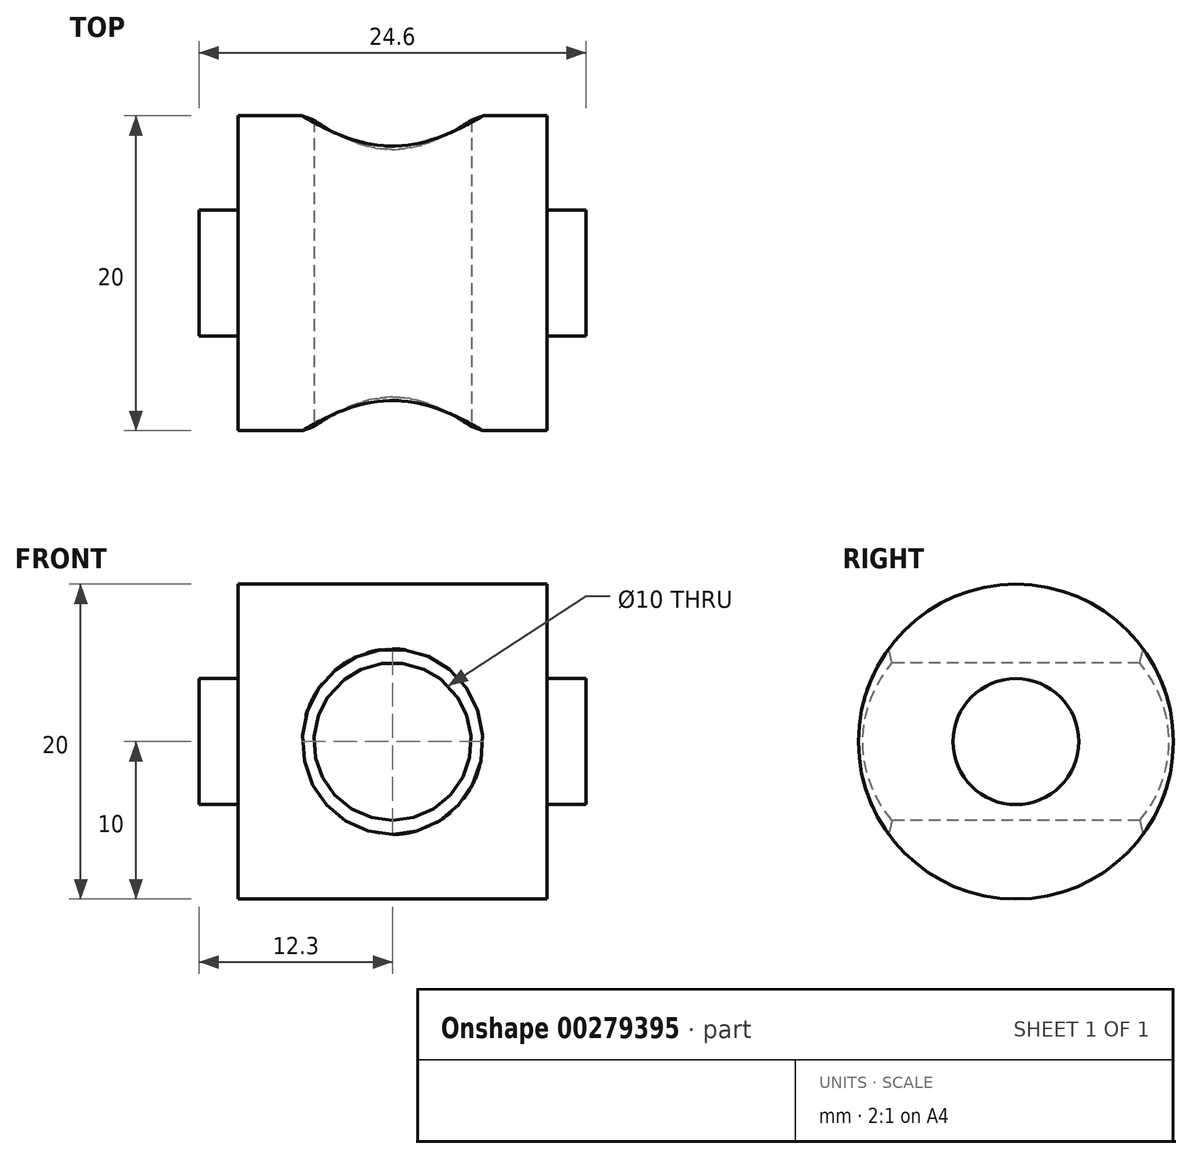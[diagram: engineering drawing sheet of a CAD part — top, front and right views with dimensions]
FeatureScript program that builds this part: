
annotation { "Feature Type Name" : "Feature", "Feature Type Description" : "" }
export const myFeature = defineFeature(function(context is Context, id is Id, definition is map)
    precondition{}
    {
        {
            var Q0;
            Q0=qCreatedBy(makeId("Front.planeOp"),FACE);
            var sketch = newSketch(context, id + "F0", { "sketchPlane" : qUnion([Q0])});
            skLineSegment(sketch, "E0", {"start": v(0, 0) * mm, "end": v(0, 34.38) * mm, "construction": true});
            skLineSegment(sketch, "E1", {"start": v(-12.3, 0) * mm, "end": v(-12.3, -4) * mm});
            skLineSegment(sketch, "E2", {"start": v(-12.3, -4) * mm, "end": v(-9.8, -4) * mm});
            skLineSegment(sketch, "E3", {"start": v(-9.8, -4) * mm, "end": v(-9.8, -10) * mm});
            skLineSegment(sketch, "E4", {"start": v(-9.8, -10) * mm, "end": v(9.8, -10) * mm});
            skLineSegment(sketch, "E5", {"start": v(9.8, -10) * mm, "end": v(9.8, -4) * mm});
            skLineSegment(sketch, "E6", {"start": v(9.8, -4) * mm, "end": v(12.3, -4) * mm});
            skLineSegment(sketch, "E7", {"start": v(12.3, -4) * mm, "end": v(12.3, 0) * mm});
            skLineSegment(sketch, "E8", {"start": v(12.3, 0) * mm, "end": v(-12.3, 0) * mm});
            skLineSegment(sketch, "E9", {"start": v(0, 0) * mm, "end": v(-39.3, 0) * mm, "construction": true});
            skSolve(sketch);
        }
        {
            var Q0;
            Q0=makeQuery(id+"F0.imprint","IMPRINT",FACE,{"disambiguationData":[TD([[makeQuery(id+"F0.imprint","IMPRINT",EDGE,{"derivedFrom":sQuery(id+"F0.wireOp",EDGE,"E1")}),1.0]])]});
            var Q1;
            Q1=sQuery(id+"F0.wireOp",EDGE,"E9");
            revolve(context, id + "F1", {"entities" : qUnion([Q0]), "axis" : qUnion([Q1]), "revolveType" : RevolveType.FULL});
        }
        {
            var Q0;
            Q0=qCreatedBy(makeId("Front.planeOp"),FACE);
            var sketch = newSketch(context, id + "F2", { "sketchPlane" : qUnion([Q0])});
            skCircle(sketch, "E10", {"center": v(0, 0) * mm, "radius": 5 * mm});
            skSolve(sketch);
        }
        {
            var Q0;
            Q0 = qSketchRegion(id + "F2", true);
            extrude(context, id + "F3", {"entities" : qUnion([Q0]), "operationType" : NewBodyOperationType.REMOVE, "endBound" : BoundingType.SYMMETRIC, "oppositeDirection" : true, "depth" : 25 * mm});
        }
        {
            var Q0;
            Q0=makeQuery(id+"F3.boolean.opBoolean","COPY",FACE,{"derivedFrom":makeQuery(id+"F3.opExtrude","SWEPT_FACE",FACE,{"disambiguationData":[OSD([sQuery(id+"F2.wireOp",EDGE,"E10")])]})});
            chamfer(context, id + "F4", {"entities" : qUnion([Q0]), "chamferType" : ChamferType.OFFSET_ANGLE, "width" : 1 * mm, "oppositeDirection" : false, "angle" : 45 * degree, "tangentPropagation" : true});
        }
    });
